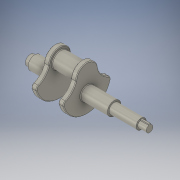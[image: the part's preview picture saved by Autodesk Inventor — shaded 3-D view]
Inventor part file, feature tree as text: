
AUTODESK INVENTOR PART (.ipt)
format: ipt  version: 2019 (Build 230136000, 136)  size: 287,232 bytes
history: native  units: mm
features: extrude x7, sketch x7, fillet x2, plane x1, mirror x1
ambient origin geometry x8: Origin, YZ Plane, XZ Plane, XY Plane, X Axis, Y Axis, Z Axis, Center Point
bodies: Solid1 (feature_tree)
feature tree (18):
  extrude  "Extrusion1"  Depth=650.0mm TaperAngle=0.0deg
  extrude  "Extrusion2"  Depth=3000.0mm TaperAngle=0.0deg
  extrude  "Extrusion3"  Depth=3250.0mm TaperAngle=0.0deg
  extrude  "Extrusion4"  Depth=2000.0mm
  plane  "Work Plane1"
  mirror  "Mirror1"
  extrude  "Extrusion5"  Depth=4000.0mm
  extrude  "Extrusion6"  Depth=4000.0mm TaperAngle=0.0deg
  extrude  "Extrusion7"  Depth=100.0mm
  fillet  "Fillet1"  [1 undecoded]
  fillet  "Fillet2"  [1 undecoded]
  sketch  "Sketch1"  dims[d1=1500.0mm d2=650.0mm d3=0.0mm]
  sketch  "Sketch2"  dims[d4=2000.0mm d5=3000.0mm d6=0.0mm]
  sketch  "Sketch3"  dims[d20=750.0mm d21=0.0mm d24=3250.0mm d25=0.0mm]
  sketch  "Sketch4"  dims[d26=-1625.0mm d27=2000.0mm]
  sketch  "Sketch5"  dims[d28=4000.0mm d29=0.0mm d30=1500.0mm]
  sketch  "Sketch6"  dims[d31=4000.0mm d32=0.0mm d37=1250.0mm d38=0.0mm]
  sketch  "Sketch7"  dims[d39=500.0mm d40=100.0mm]
note: 2 required parameter values undecoded (feature->parameter linkage not recoverable at this tier; creation-order binding heuristic only, values carry confidence <= 0.55)
